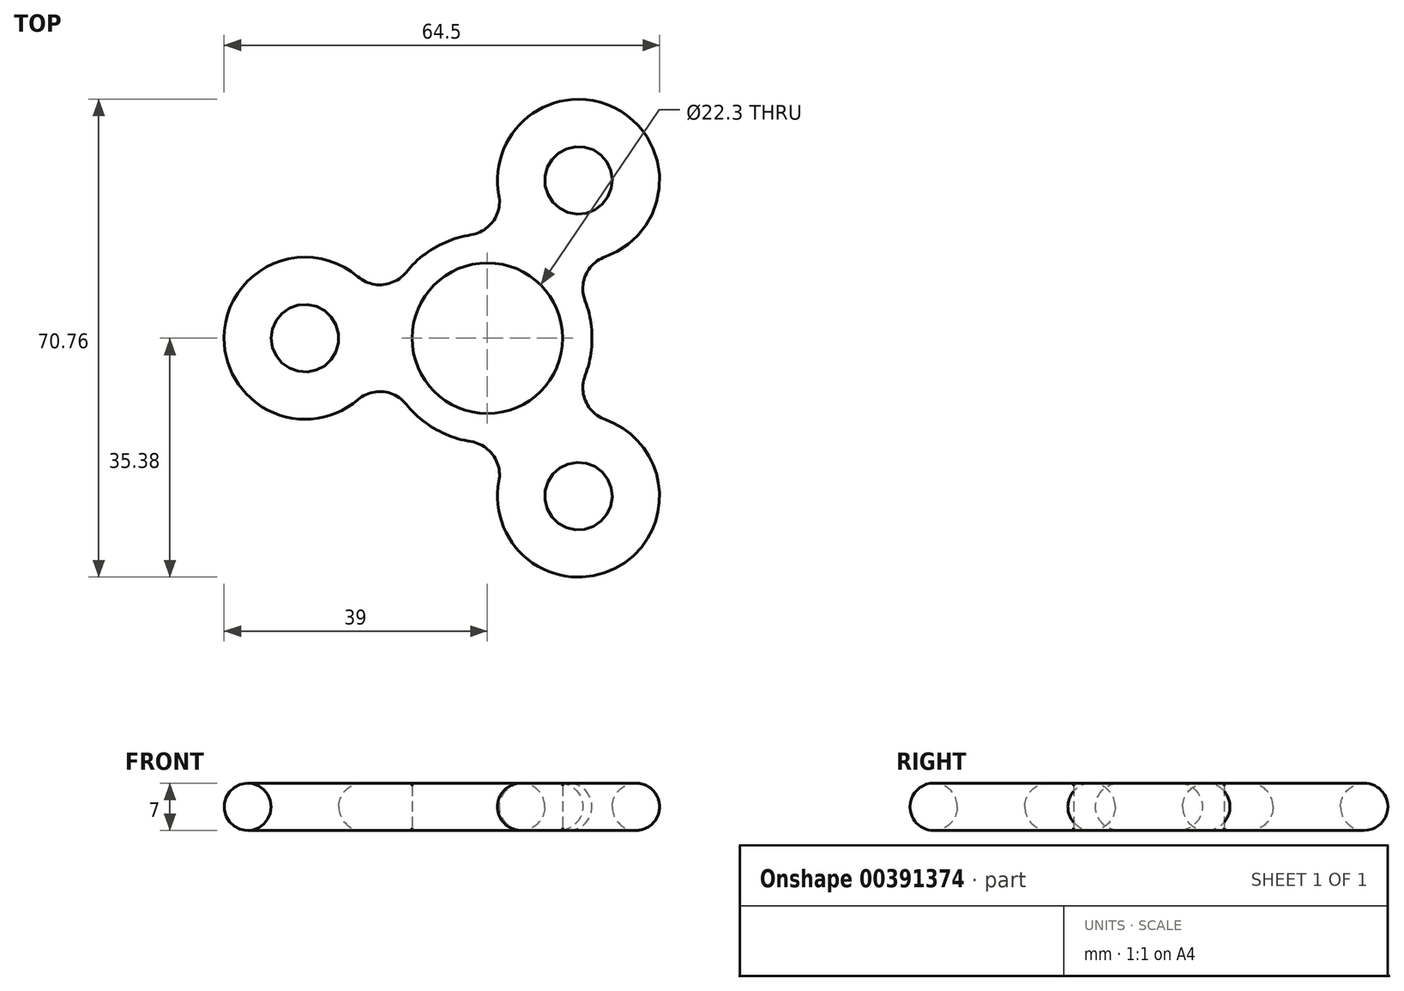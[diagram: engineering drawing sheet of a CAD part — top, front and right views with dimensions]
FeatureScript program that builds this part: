
annotation { "Feature Type Name" : "Feature", "Feature Type Description" : "" }
export const myFeature = defineFeature(function(context is Context, id is Id, definition is map)
    precondition{}
    {
        {
            var Q0;
            Q0=qCreatedBy(makeId("Top.planeOp"),FACE);
            var sketch = newSketch(context, id + "F0", { "sketchPlane" : qUnion([Q0])});
            skArc(sketch, "E0", {"start": v(-12.05, -9.76) * mm, "mid": v(-7.75, -13.42) * mm, "end": v(-2.43, -15.3) * mm});
            skArc(sketch, "E1.trimOffspring", {"start": v(15.5, 0) * mm, "mid": v(15.24, 2.82) * mm, "end": v(14.47, 5.55) * mm});
            skCircle(sketch, "E2", {"center": v(0, 0) * mm, "radius": 11.15 * mm});
            skArc(sketch, "E3.trimOffspring", {"start": v(-2.43, 15.3) * mm, "mid": v(-7.75, 13.42) * mm, "end": v(-12.05, 9.76) * mm});
            skArc(sketch, "E4.trimOffspring", {"start": v(14.47, -5.55) * mm, "mid": v(15.24, -2.82) * mm, "end": v(15.5, 0) * mm});
            skCircle(sketch, "E5", {"center": v(-27, 0) * mm, "radius": 5 * mm});
            skArc(sketch, "E6", {"start": v(-19.19, 9.1) * mm, "mid": v(-39, 0) * mm, "end": v(-19.19, -9.1) * mm});
            skArc(sketch, "E7", {"start": v(-19.19, 9.1) * mm, "mid": v(-15.48, 7.92) * mm, "end": v(-12.05, 9.76) * mm});
            skArc(sketch, "E8", {"start": v(-12.05, -9.76) * mm, "mid": v(-15.48, -7.92) * mm, "end": v(-19.19, -9.1) * mm});
            skArc(sketch, "E9.1.0", {"start": v(1.7, -21.17) * mm, "mid": v(19.5, -33.77) * mm, "end": v(17.48, -12.06) * mm});
            skCircle(sketch, "E9.1.1", {"center": v(13.5, -23.38) * mm, "radius": 5 * mm});
            skArc(sketch, "E9.1.2", {"start": v(14.47, -5.55) * mm, "mid": v(14.6, -9.44) * mm, "end": v(17.48, -12.06) * mm});
            skArc(sketch, "E9.1.3", {"start": v(1.7, -21.17) * mm, "mid": v(0.88, -17.37) * mm, "end": v(-2.43, -15.3) * mm});
            skArc(sketch, "E9.2.0", {"start": v(17.48, 12.06) * mm, "mid": v(19.5, 33.77) * mm, "end": v(1.7, 21.17) * mm});
            skCircle(sketch, "E9.2.1", {"center": v(13.5, 23.38) * mm, "radius": 5 * mm});
            skArc(sketch, "E9.2.2", {"start": v(-2.43, 15.3) * mm, "mid": v(0.88, 17.37) * mm, "end": v(1.7, 21.17) * mm});
            skArc(sketch, "E9.2.3", {"start": v(17.48, 12.06) * mm, "mid": v(14.6, 9.44) * mm, "end": v(14.47, 5.55) * mm});
            skSolve(sketch);
        }
        {
            var Q0;
            Q0=qSketchRegion(id+"F0",true);
            extrude(context, id + "F1", {"entities" : qUnion([Q0]), "depth" : 7 * mm});
        }
        {
            var Q0;
            Q0=makeQuery(id+"F1.opExtrude","SWEPT_FACE",FACE,{"disambiguationData":[OSD([sQuery(id+"F0.wireOp",EDGE,"E2")])]});
            fillet(context, id + "F2", {"entities" : qUnion([Q0]), "radius" : .4 * mm, "tangentPropagation" : true, "allowEdgeOverflow" : false});
        }
        {
            var Q0;
            Q0=makeQuery(id+"F1.opExtrude","CAP_FACE",FACE,{"disambiguationData":[OSD([sQuery(id+"F0.wireOp",EDGE,"E0"),sQuery(id+"F0.wireOp",EDGE,"E1.trimOffspring"),sQuery(id+"F0.wireOp",EDGE,"E2"),sQuery(id+"F0.wireOp",EDGE,"E3.trimOffspring"),sQuery(id+"F0.wireOp",EDGE,"E4.trimOffspring"),sQuery(id+"F0.wireOp",EDGE,"E5"),sQuery(id+"F0.wireOp",EDGE,"E6"),sQuery(id+"F0.wireOp",EDGE,"E7"),sQuery(id+"F0.wireOp",EDGE,"E8"),sQuery(id+"F0.wireOp",EDGE,"E9.1.0"),sQuery(id+"F0.wireOp",EDGE,"E9.1.1"),sQuery(id+"F0.wireOp",EDGE,"E9.1.2"),sQuery(id+"F0.wireOp",EDGE,"E9.1.3"),sQuery(id+"F0.wireOp",EDGE,"E9.2.0"),sQuery(id+"F0.wireOp",EDGE,"E9.2.1"),sQuery(id+"F0.wireOp",EDGE,"E9.2.2"),sQuery(id+"F0.wireOp",EDGE,"E9.2.3")])],"isStart":false});
            var Q1;
            Q1=makeQuery(id+"F1.opExtrude","CAP_FACE",FACE,{"disambiguationData":[OSD([sQuery(id+"F0.wireOp",EDGE,"E0"),sQuery(id+"F0.wireOp",EDGE,"E1.trimOffspring"),sQuery(id+"F0.wireOp",EDGE,"E2"),sQuery(id+"F0.wireOp",EDGE,"E3.trimOffspring"),sQuery(id+"F0.wireOp",EDGE,"E4.trimOffspring"),sQuery(id+"F0.wireOp",EDGE,"E5"),sQuery(id+"F0.wireOp",EDGE,"E6"),sQuery(id+"F0.wireOp",EDGE,"E7"),sQuery(id+"F0.wireOp",EDGE,"E8"),sQuery(id+"F0.wireOp",EDGE,"E9.1.0"),sQuery(id+"F0.wireOp",EDGE,"E9.1.1"),sQuery(id+"F0.wireOp",EDGE,"E9.1.2"),sQuery(id+"F0.wireOp",EDGE,"E9.1.3"),sQuery(id+"F0.wireOp",EDGE,"E9.2.0"),sQuery(id+"F0.wireOp",EDGE,"E9.2.1"),sQuery(id+"F0.wireOp",EDGE,"E9.2.2"),sQuery(id+"F0.wireOp",EDGE,"E9.2.3")])],"isStart":true});
            fillet(context, id + "F3", {"entities" : qUnion([Q0, Q1]), "radius" : 3.5 * mm, "tangentPropagation" : true, "allowEdgeOverflow" : false});
        }
    });
